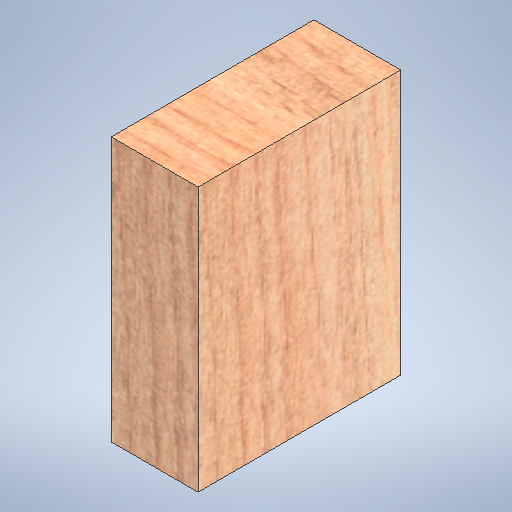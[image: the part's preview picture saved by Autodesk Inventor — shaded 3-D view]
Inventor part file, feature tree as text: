
AUTODESK INVENTOR PART (.ipt)
format: ipt  version: 2025.1 (Build 291241020, 241B)  size: 467,456 bytes
history: native  units: in
note: dims shown in document units (in); Inventor stores cm internally (conversion verified against a paired STEP export)
features: extrude x1, sketch x1
ambient origin geometry x8: Origin, YZ Plane, XZ Plane, XY Plane, X Axis, Y Axis, Z Axis, Center Point
bodies: Solid1 (feature_tree)
feature tree (2):
  extrude  "Extrusion1"  Depth=1.5in
  sketch  "Sketch1"  dims[d0=3.5in d1=1.5in d2=4.5625in d3=0.0in]
